# Revit family: JOMA_419 & 429
name_source: partatom
category: Structural Connections
revit_build: Autodesk Revit Structure 2012 (Build: 20110309_2315(x64)
units: mm (PartAtom-declared; Revit-internal decimal feet)

## types (2) — shared parameters
Länk Joma Dimensioneringsverktyg = http://www.joma.se
Material = Varmförzinkad stålplåt
b = 40 mm  [stored 0.131234 ft]
ir = 2.562 mm  [stored 0.00840551 ft]
l = 50 mm  [stored 0.164042 ft]
t = 2 mm  [stored 0.00656168 ft]
yr = 4.562 mm  [stored 0.0149672 ft]
zero-valued in all types: Default Elevation

## per-type parameters (varying)
| type | Typ | Vikt | Vinkelbeslag 419 | Vinkelbeslag 429 | h |
| 4190000 | VINKEL 419 | 0,141 | Yes | No | 190 mm |
| 4290000 | VINKEL 429 | 0,202 | No | Yes | 290 mm  [stored 0.951444 ft] |

note: [stored X ft] marks values corroborated as IEEE doubles in the binary element streams (Revit-internal decimal feet)

## geometry (parser evidence)
native form markers: Sweep x2
no freeform markers — native parametric forms only
